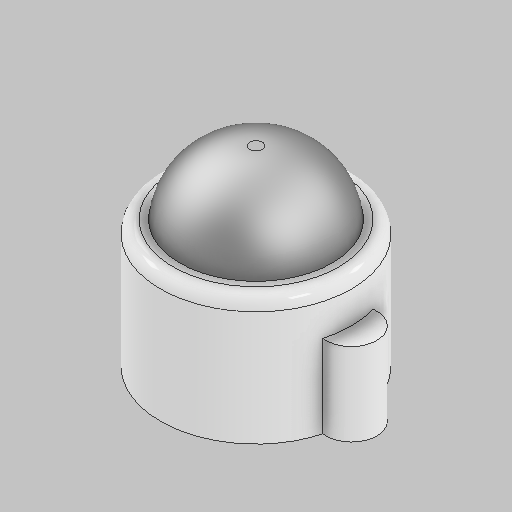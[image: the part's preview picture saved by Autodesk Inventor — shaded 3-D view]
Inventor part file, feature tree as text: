
AUTODESK INVENTOR PART (.ipt)
format: ipt  version: 2025 (Build 290162010, 162A)  size: 182,784 bytes
history: native  units: mm
features: other x5, extrude x3, sketch x3, fillet x2
ambient origin geometry x8: Origin, YZ Plane, XZ Plane, XY Plane, X Axis, Y Axis, Z Axis, Center Point
bodies: Body1 (feature_tree)
feature tree (13):
  other  "Sólido1"
  extrude  "Extrusión1"  TaperAngle=0.0deg  [1 undecoded]
  fillet  "Empalme1"  Radius=12.0mm
  extrude  "Extrusión2"  Depth=5.5mm
  fillet  "Empalme2"  Radius=15.0mm
  extrude  "Extrusión3"  Depth=1.0mm
  sketch  "Boceto1"  dims[d0=0.0mm d1=0.0mm d2=12.0mm]
  sketch  "Boceto2"  dims[d3=15.0mm d4=0.0mm d5=5.5mm d6=15.0mm]
  sketch  "Boceto3"  dims[d7=10.0mm d8=0.0mm d9=1.0mm d10=7.5mm d12=4.0mm d14=7.5mm d15=4.0mm d16=6.5mm d17=0.0mm d11=0.872665mm d13=0.872665mm]
  other  "Finish1"
  other  "Finish2"
  other  "Finish3"
  other  "Finish4"
note: 1 required parameter value undecoded (feature->parameter linkage not recoverable at this tier; creation-order binding heuristic only, values carry confidence <= 0.55)
